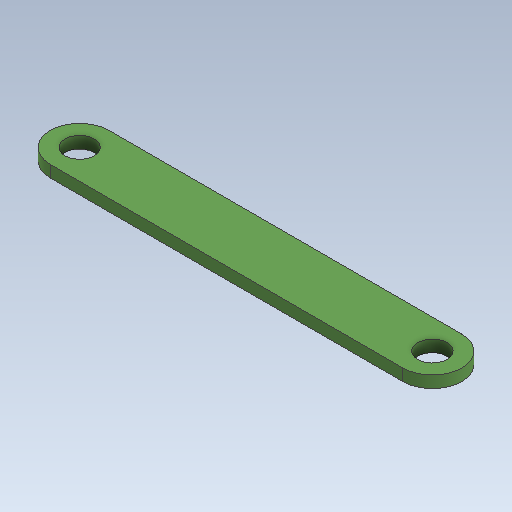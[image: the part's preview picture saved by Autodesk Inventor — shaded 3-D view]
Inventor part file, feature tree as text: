
AUTODESK INVENTOR PART (.ipt)
format: ipt  version: 2020.1 (Build 241239000, 239)  size: 118,272 bytes
history: native  units: in
note: dims shown in document units (in); Inventor stores cm internally (conversion verified against a paired STEP export)
features: extrude x1, sketch x1
ambient origin geometry x8: Origin, YZ Plane, XZ Plane, XY Plane, X Axis, Y Axis, Z Axis, Center Point
bodies: Solid1 (feature_tree)
feature tree (2):
  extrude  "Extrusion1"  Depth=10.0in
  sketch  "Sketch1"  dims[d0=60.0in d1=10.0in d2=5.0in d3=5.0in d4=2.0in d5=0.0in]
